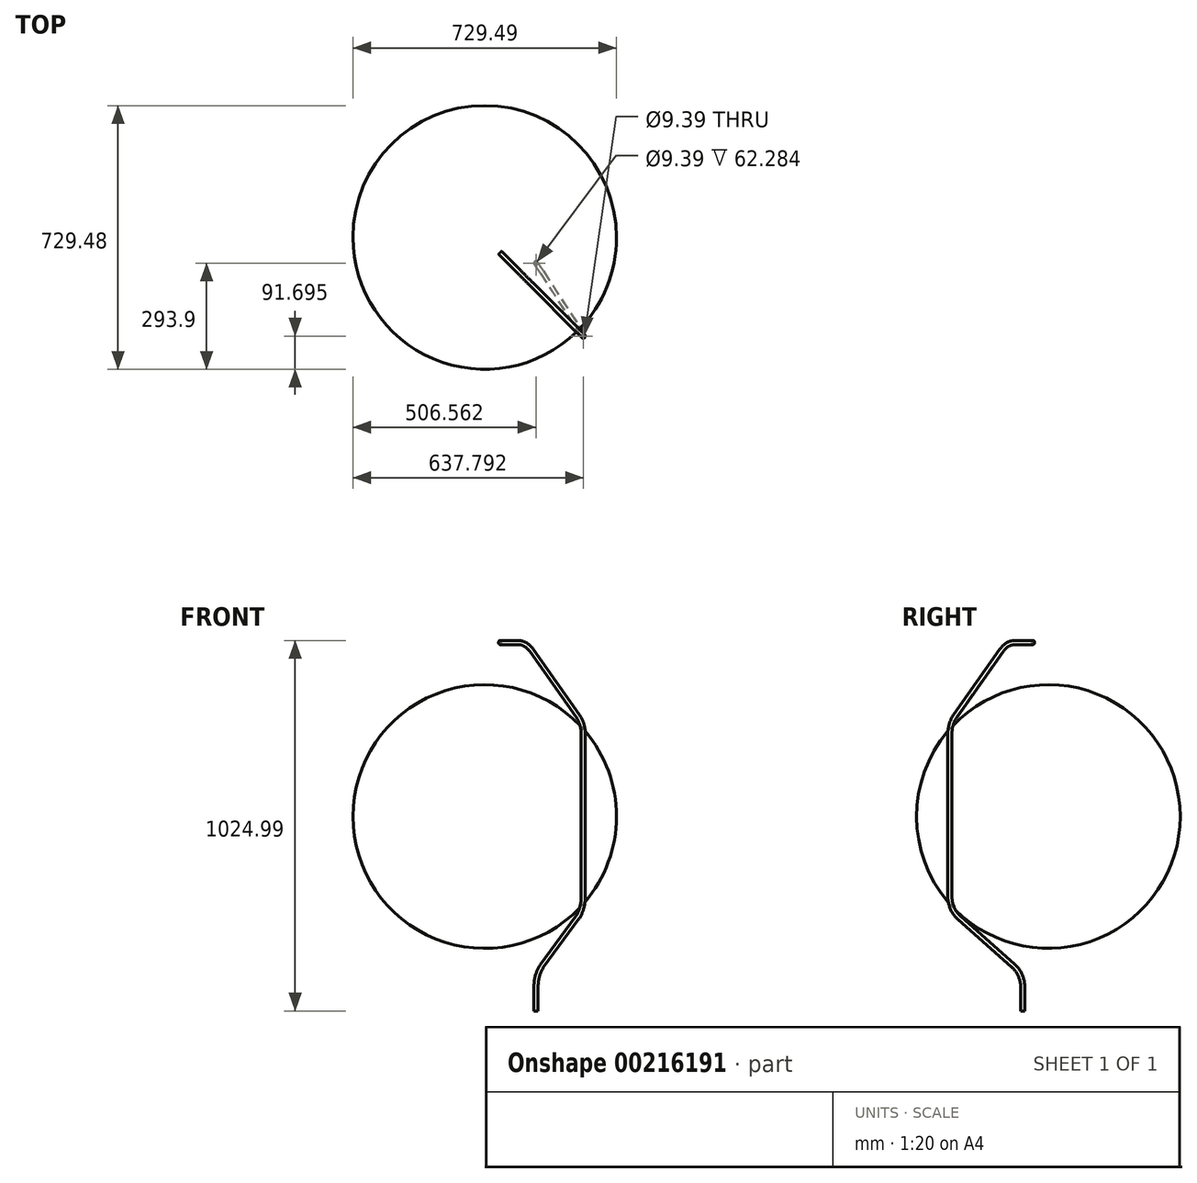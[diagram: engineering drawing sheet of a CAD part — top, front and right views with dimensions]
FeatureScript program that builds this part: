
annotation { "Feature Type Name" : "Feature", "Feature Type Description" : "" }
export const myFeature = defineFeature(function(context is Context, id is Id, definition is map)
    precondition{}
    {
        {
            var Q0;
            Q0=qCreatedBy(makeId("Top.planeOp"),FACE);
            var sketch = newSketch(context, id + "F0", { "sketchPlane" : qUnion([Q0])});
            skLineSegment(sketch, "E0", {"start": v(0, 0) * mm, "end": v(-143.34, 0) * mm});
            skLineSegment(sketch, "E1", {"start": v(-143.34, 0) * mm, "end": v(-143.34, 215.7) * mm});
            skLineSegment(sketch, "E2", {"start": v(0, 0) * mm, "end": v(-185.8, 0) * mm});
            skLineSegment(sketch, "E3", {"start": v(-185.8, 0) * mm, "end": v(-185.8, 258.16) * mm});
            skLineSegment(sketch, "E4", {"start": v(0, 0) * mm, "end": v(-43.98, 0) * mm});
            skPoint(sketch, "E4.endSnap0", {"position": v(-92.9, 0) * mm});
            skLineSegment(sketch, "E5", {"start": v(-43.98, 0) * mm, "end": v(-43.98, 187.32) * mm});
            skSolve(sketch);
        }
        {
            var Q0;
            Q0=sQuery(id+"F0.wireOp",EDGE,"E1");
            cPlane(context, id + "F1", {"entities" : qUnion([Q0]), "cplaneType" : CPlaneType.LINE_ANGLE, "offset" : 25.4 * mm, "angle" : 90 * degree, "width" : 152.4 * mm, "height" : 152.4 * mm});
        }
        {
            var Q0;
            Q0=qCreatedBy(id+"F1.planeOp",FACE);
            var sketch = newSketch(context, id + "F2", { "sketchPlane" : qUnion([Q0])});
            skLineSegment(sketch, "E6", {"start": v(215.7, 0) * mm, "end": v(215.7, 797.23) * mm});
            skSolve(sketch);
        }
        {
            var Q0;
            Q0=sQuery(id+"F2.wireOp",EDGE,"E6");
            cPlane(context, id + "F3", {"entities" : qUnion([Q0]), "cplaneType" : CPlaneType.LINE_ANGLE, "offset" : 25.4 * mm, "angle" : 135 * degree, "width" : 152.4 * mm, "height" : 152.4 * mm});
        }
        {
            var Q0;
            Q0=sQuery(id+"F0.wireOp",EDGE,"E3");
            cPlane(context, id + "F4", {"entities" : qUnion([Q0]), "cplaneType" : CPlaneType.LINE_ANGLE, "offset" : 25.4 * mm, "angle" : 90 * degree, "width" : 152.4 * mm, "height" : 152.4 * mm});
        }
        {
            var Q0;
            Q0=qCreatedBy(id+"F4.planeOp",FACE);
            var sketch = newSketch(context, id + "F5", { "sketchPlane" : qUnion([Q0])});
            skLineSegment(sketch, "E7", {"start": v(258.16, 0) * mm, "end": v(258.16, 315.75) * mm});
            skLineSegment(sketch, "E8", {"start": v(258.16, 315.75) * mm, "end": v(283.56, 315.75) * mm});
            skSolve(sketch);
        }
        {
            var Q0;
            Q0=sQuery(id+"F5.wireOp",EDGE,"E8");
            cPlane(context, id + "F6", {"entities" : qUnion([Q0]), "cplaneType" : CPlaneType.LINE_ANGLE, "offset" : 25.4 * mm, "angle" : 0 * degree, "width" : 152.4 * mm, "height" : 152.4 * mm});
        }
        {
            var Q0;
            Q0=qCreatedBy(id+"F6.planeOp",FACE);
            var sketch = newSketch(context, id + "F7", { "sketchPlane" : qUnion([Q0])});
            skArc(sketch, "E9", {"start": v(-550.54, 258.16) * mm, "mid": v(-185.8, -106.58) * mm, "end": v(178.95, 258.16) * mm});
            skLineSegment(sketch, "E10", {"start": v(-185.8, 258.16) * mm, "end": v(-550.54, 258.16) * mm});
            skLineSegment(sketch, "E11", {"start": v(-550.54, 258.16) * mm, "end": v(178.95, 258.16) * mm});
            skSolve(sketch);
        }
        {
            var Q0;
            Q0=sQuery(id+"F0.wireOp",EDGE,"E5");
            cPlane(context, id + "F8", {"entities" : qUnion([Q0]), "cplaneType" : CPlaneType.LINE_ANGLE, "offset" : 25.4 * mm, "angle" : 90 * degree, "width" : 152.4 * mm, "height" : 152.4 * mm});
        }
        {
            var Q0;
            Q0=qCreatedBy(id+"F8.planeOp",FACE);
            var sketch = newSketch(context, id + "F9", { "sketchPlane" : qUnion([Q0])});
            skLineSegment(sketch, "E12", {"start": v(187.32, 0) * mm, "end": v(187.32, -222.05) * mm});
            skLineSegment(sketch, "E13", {"start": v(187.32, -222.05) * mm, "end": v(161.92, -222.05) * mm});
            skSolve(sketch);
        }
        {
            var Q0;
            Q0=sQuery(id+"F9.wireOp",EDGE,"E13");
            cPlane(context, id + "F10", {"entities" : qUnion([Q0]), "cplaneType" : CPlaneType.LINE_ANGLE, "offset" : 25.4 * mm, "angle" : 0 * degree, "width" : 152.4 * mm, "height" : 152.4 * mm});
        }
        {
            var Q0;
            Q0=qCreatedBy(id+"F10.planeOp",FACE);
            var sketch = newSketch(context, id + "F11", { "sketchPlane" : qUnion([Q0])});
            skCircle(sketch, "E14", {"center": v(-43.98, -187.32) * mm, "radius": 5.7 * mm});
            skSolve(sketch);
        }
        {
            var Q0;
            {var subQ0=sQuery(id+"F7.wireOp",EDGE,"E9");Q0=makeQuery(id+"F7.imprint","IMPRINT",FACE,{"disambiguationData":[TD([[makeQuery(id+"F7.imprint","IMPRINT",EDGE,{"derivedFrom":subQ0}),1.0]])]});}
            var Q1;
            Q1=sQuery(id+"F7.wireOp",EDGE,"E11");
            revolve(context, id + "F12", {"entities" : qUnion([Q0]), "axis" : qUnion([Q1]), "revolveType" : RevolveType.FULL});
        }
        {
            var Q0;
            Q0=sQuery(id+"F2.wireOp",EDGE,"E6");
            cPlane(context, id + "F13", {"entities" : qUnion([Q0]), "cplaneType" : CPlaneType.LINE_ANGLE, "offset" : 25.4 * mm, "angle" : 225 * degree, "width" : 152.4 * mm, "height" : 152.4 * mm});
        }
        {
            var Q0;
            Q0=qCreatedBy(id+"F13.planeOp",FACE);
            var sketch = newSketch(context, id + "F14", { "sketchPlane" : qUnion([Q0])});
            skLineSegment(sketch, "E15", {"start": v(-253.88, 797.23) * mm, "end": v(-183.85, 797.23) * mm});
            skLineSegment(sketch, "E16", {"start": v(-129.97, 774.91) * mm, "end": v(49.9, 595.04) * mm});
            skLineSegment(sketch, "E17", {"start": v(-313.92, 315.75) * mm, "end": v(-75.1, 315.75) * mm});
            skLineSegment(sketch, "E18", {"start": v(72.22, 541.16) * mm, "end": v(72.22, 315.75) * mm});
            skPoint(sketch, "E19.visualSharp", {"position": v(-152.28, 797.23) * mm});
            skArc(sketch, "E19.filletArc", {"start": v(-129.97, 774.91) * mm, "mid": v(-154.69, 791.43) * mm, "end": v(-183.85, 797.23) * mm});
            skPoint(sketch, "E20.visualSharp", {"position": v(72.22, 572.73) * mm});
            skArc(sketch, "E20.filletArc", {"start": v(72.22, 541.16) * mm, "mid": v(66.42, 570.32) * mm, "end": v(49.9, 595.04) * mm});
            skPoint(sketch, "E21.MirrorCS.end.orphan", {"position": v(72.22, 58.77) * mm});
            skPoint(sketch, "E21.MirrorCS.start.orphan", {"position": v(-152.28, -165.74) * mm});
            skPoint(sketch, "E22.MirrorCS.end.orphan", {"position": v(72.22, 315.75) * mm});
            skSolve(sketch);
        }
        {
            var Q0;
            Q0=sQuery(id+"F11.wireOp",VERTEX,"E14.center");
            var Q1;
            Q1=sQuery(id+"F14.wireOp",VERTEX,"E21.MirrorCS.end.orphan");
            var Q2;
            Q2=sQuery(id+"F0.wireOp",VERTEX,"E5.end");
            cPlane(context, id + "F15", {"entities" : qUnion([Q0, Q1, Q2]), "cplaneType" : CPlaneType.THREE_POINT, "offset" : 25.4 * mm, "width" : 152.4 * mm, "height" : 152.4 * mm});
        }
        {
            var Q0;
            Q0=qCreatedBy(id+"F15.planeOp",FACE);
            var sketch = newSketch(context, id + "F16", { "sketchPlane" : qUnion([Q0])});
            skLineSegment(sketch, "E23", {"start": v(181.07, -222.05) * mm, "end": v(181.07, -158.75) * mm});
            skPoint(sketch, "E24.visualSharp", {"position": v(181.07, -120.45) * mm});
            skArc(sketch, "E24.filletArc", {"start": v(181.07, -158.75) * mm, "mid": v(172.95, -124.53) * mm, "end": v(150.33, -97.6) * mm});
            skSolve(sketch);
        }
        {
            var Q0;
            Q0=qCreatedBy(id+"F15.planeOp",FACE);
            var sketch = newSketch(context, id + "F17", { "sketchPlane" : qUnion([Q0])});
            skLineSegment(sketch, "E25", {"start": v(-59.99, 315.75) * mm, "end": v(-59.99, 97.07) * mm});
            skLineSegment(sketch, "E26", {"start": v(-29.25, 35.92) * mm, "end": v(150.33, -97.6) * mm});
            skPoint(sketch, "E27.visualSharp", {"position": v(-59.99, 58.77) * mm});
            skArc(sketch, "E27.filletArc", {"start": v(-59.99, 97.07) * mm, "mid": v(-51.87, 62.85) * mm, "end": v(-29.25, 35.92) * mm});
            skSolve(sketch);
        }
        {
            var Q0;
            Q0=makeQuery(id+"F11.imprint","IMPRINT",FACE,{"disambiguationData":[TD([[makeQuery(id+"F11.imprint","IMPRINT",EDGE,{"derivedFrom":sQuery(id+"F11.wireOp",EDGE,"E14")}),1.0]])]});
            var Q1;
            Q1=sQuery(id+"F16.wireOp",EDGE,"E23");
            var Q2;
            Q2=sQuery(id+"F16.wireOp",EDGE,"E24.filletArc");
            var Q3;
            Q3=sQuery(id+"F17.wireOp",EDGE,"E26");
            var Q4;
            Q4=sQuery(id+"F17.wireOp",EDGE,"E27.filletArc");
            var Q5;
            Q5=sQuery(id+"F17.wireOp",EDGE,"E25");
            var Q6;
            Q6=sQuery(id+"F14.wireOp",EDGE,"E18");
            var Q7;
            Q7=sQuery(id+"F14.wireOp",EDGE,"E20.filletArc");
            var Q8;
            Q8=sQuery(id+"F14.wireOp",EDGE,"E16");
            var Q9;
            Q9=sQuery(id+"F14.wireOp",EDGE,"E19.filletArc");
            var Q10;
            Q10=sQuery(id+"F14.wireOp",EDGE,"E15");
            sweep(context, id + "F18", {"profiles" : qUnion([Q0]), "path" : qUnion([Q1, Q2, Q3, Q4, Q5, Q6, Q7, Q8, Q9, Q10])});
        }
        {
            var Q0;
            Q0=makeQuery(id+"F18.opSweep","CAP_FACE",FACE,{"disambiguationData":[OSD([sQuery(id+"F11.wireOp",EDGE,"E14"),sQuery(id+"F14.wireOp",VERTEX,"E15.start")])],"isStart":false});
            shell(context, id + "F19", {"entities" : qUnion([Q0]), "thickness" : 1.02 * mm});
        }
    });
